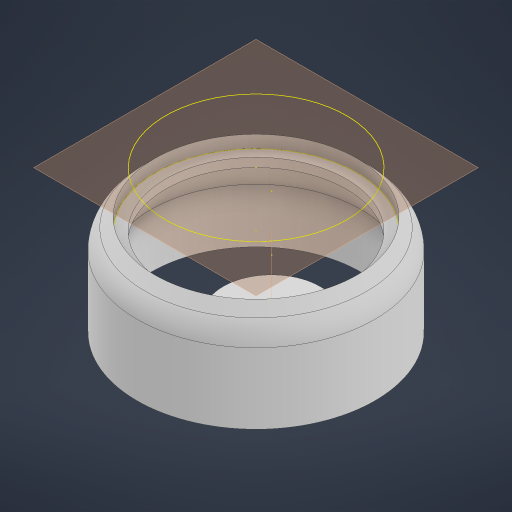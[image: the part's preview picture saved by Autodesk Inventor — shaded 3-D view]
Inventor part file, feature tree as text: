
AUTODESK INVENTOR PART (.ipt)
format: ipt  version: 2023 (Build 270158030, 158C)  size: 305,152 bytes
history: native  units: mm
features: sketch x9, extrude x6, direct_edit x4, move_body x3, shell x2, chamfer x2, fillet x2, other x2, plane x1, projected_geometry x1
ambient origin geometry x8: Origin, YZ Plane, XZ Plane, XY Plane, X Axis, Y Axis, Z Axis, Center Point
bodies: Solid1 (feature_tree)
feature tree (32):
  extrude  "Extrusion1"  Depth=38.0mm
  extrude  "Extrusion2"  Depth=33.5mm
  shell  "Shell1"  Thickness=4.1mm
  extrude  "Extrusion3"  Depth=10.0mm
  direct_edit  "Direct Edit1"
  chamfer  "Chamfer1"  Distance=8.25mm
  fillet  "Fillet3"  Radius=1.0mm
  other  "Work Axis1"
  sketch  "Sketch9"  dims[d25=2.5mm d26=2.0mm d27=45.0deg d28=4.0mm]
  extrude  "Extrusion8"  Depth=4.0mm
  direct_edit  "Direct Edit4"
  extrude  "Extrusion9"  TaperAngle=0.0deg  [1 undecoded]
  fillet  "Fillet6"  Radius=13.6mm
  shell  "Shell2"  Thickness=2.0mm
  direct_edit  "Direct Edit5"
  extrude  "Extrusion10"  Depth=1.0mm
  chamfer  "Chamfer2"  [1 undecoded]
  direct_edit  "Direct Edit6"
  sketch  "Sketch13"  dims[d49=2.0mm d50=0.0mm]
  plane  "Work Plane2"
  sketch  "Sketch14"  dims[d51=2.0mm d52=2.0mm d53=60.0deg d54=0.0mm d55=0.0mm d56=-0.75mm d57=7.75mm d32=0.5mm d33=0.872665mm d34=0.5mm]
  sketch  "Sketch1"  dims[d0=11.6mm d1=38.0mm]
  sketch  "Sketch2"  dims[d2=38.5mm d3=33.5mm d4=4.1mm d5=0.0mm]
  sketch  "Sketch3"  dims[d6=10.0mm d7=0.0mm d8=1.0mm d9=8.25mm d10=0.0mm d16=1.0mm]
  sketch  "Sketch10"  dims[d35=2.0mm d36=0.0mm d37=0.0mm d38=0.0mm d39=-7.0mm d40=13.6mm d41=2.0mm d42=0.0mm]
  projected_geometry  "Projected Loop2"
  sketch  "Sketch11"  dims[d43=2.0mm d44=1.0mm d45=-1.15mm d46=0.0mm d47=0.0mm]
  sketch  "Sketch12"  dims[d48=2.0mm]
  other  "Size1"
  move_body  "Move3"
  move_body  "Move4"
  move_body  "Move5"
note: 2 required parameter values undecoded (feature->parameter linkage not recoverable at this tier; creation-order binding heuristic only, values carry confidence <= 0.55)
